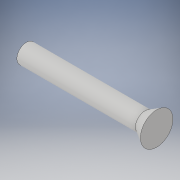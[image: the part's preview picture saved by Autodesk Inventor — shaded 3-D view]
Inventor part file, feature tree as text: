
AUTODESK INVENTOR PART (.ipt)
format: ipt  version: 2018.3 (Build 223284000, 284)  size: 101,888 bytes
history: native  units: in
note: dims shown in document units (in); Inventor stores cm internally (conversion verified against a paired STEP export)
features: revolve x1, sketch x1
ambient origin geometry x8: Origin, YZ Plane, XZ Plane, XY Plane, X Axis, Y Axis, Z Axis, Center Point
bodies: Solid1 (feature_tree)
feature tree (2):
  revolve  "Revolution1"  Angle=60.0deg
  sketch  "Sketch1"  dims[d0=0.1in d1=60.0deg d2=0.41in d3=0.1in d4=90.0deg]
